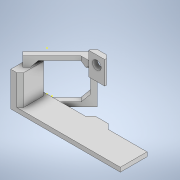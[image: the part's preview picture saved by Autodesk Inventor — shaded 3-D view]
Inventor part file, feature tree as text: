
AUTODESK INVENTOR PART (.ipt)
format: ipt  version: 2021.2 (Build 252289000, 289)  size: 262,656 bytes
history: native  units: in
note: dims shown in document units (in); Inventor stores cm internally (conversion verified against a paired STEP export)
features: sketch x19, extrude x14, chamfer x4
ambient origin geometry x8: Origin, YZ Plane, XZ Plane, XY Plane, X Axis, Y Axis, Z Axis, Center Point
bodies: Solid1 (feature_tree)
feature tree (37):
  extrude  "Extrusion1"  Depth=0.16in
  extrude  "Extrusion2"  Depth=1.0in
  chamfer  "Chamfer1"  Distance=0.1875in
  extrude  "Extrusion3"  Depth=0.5625in TaperAngle=0.0deg
  extrude  "Extrusion4"  Depth=0.5625in TaperAngle=0.0deg
  sketch  "Sketch5"  dims[d9=0.125in d10=0.125in d11=45.0deg d12=0.5625in d13=0.0in]
  chamfer  "Chamfer2"  Distance=0.125in Angle=45.0deg
  sketch  "Sketch6"  dims[d14=0.33in d15=0.5625in d16=0.0in d17=0.125in d18=0.125in d19=45.0deg]
  extrude  "Extrusion5"  Depth=0.816in
  sketch  "Sketch8"  dims[d23=0.1in d24=0.0in d26=0.2875in d27=0.0in]
  extrude  "Extrusion6"  Depth=0.1in TaperAngle=0.0deg
  extrude  "Extrusion7"  Depth=1.7875in TaperAngle=0.0deg
  sketch  "Sketch11"  dims[d36=21112.9in d37=0.0in d38=1.5in d39=0.0in]
  extrude  "Extrusion8"  Depth=0.35in TaperAngle=0.0deg
  extrude  "Extrusion9"  Depth=1.5in TaperAngle=0.0deg
  extrude  "Extrusion10"  Depth=1.01in TaperAngle=0.0deg
  extrude  "Extrusion11"  Depth=0.1875in TaperAngle=45.0deg
  sketch  "Sketch16"
  extrude  "Extrusion12"  [1 undecoded]
  extrude  "Extrusion13"  [1 undecoded]
  extrude  "Extrusion14"  [1 undecoded]
  chamfer  "Chamfer3"  [1 undecoded]
  chamfer  "Chamfer4"  [1 undecoded]
  sketch  "Sketch1"  dims[d0=3.75in d1=0.16in]
  sketch  "Sketch2"  dims[d2=1.0in d3=0.0in d4=0.3in]
  sketch  "Sketch3"  dims[d5=0.3in]
  sketch  "Sketch4"  dims[d6=1.8in d7=0.1875in d8=0.0in]
  sketch  "Sketch7"  dims[d20=0.5625in d21=0.0in d22=0.816in]
  sketch  "Sketch9"  dims[d28=0.9125in d29=0.0in d30=1.7875in d31=0.0in]
  sketch  "Sketch10"  dims[d32=0.225in d33=0.0in d34=0.35in d35=0.0in]
  sketch  "Sketch12"  dims[d41=0.16in d42=1.01in d43=0.0in]
  sketch  "Sketch13"  dims[d44=0.25in d45=0.125in d46=45.0deg d47=0.1875in d48=0.125in d49=45.0deg]
  sketch  "Sketch14"
  sketch  "Sketch15"
  sketch  "Sketch17"
  sketch  "Sketch18"
  sketch  "Sketch19"
note: 5 required parameter values undecoded (feature->parameter linkage not recoverable at this tier; creation-order binding heuristic only, values carry confidence <= 0.55)
